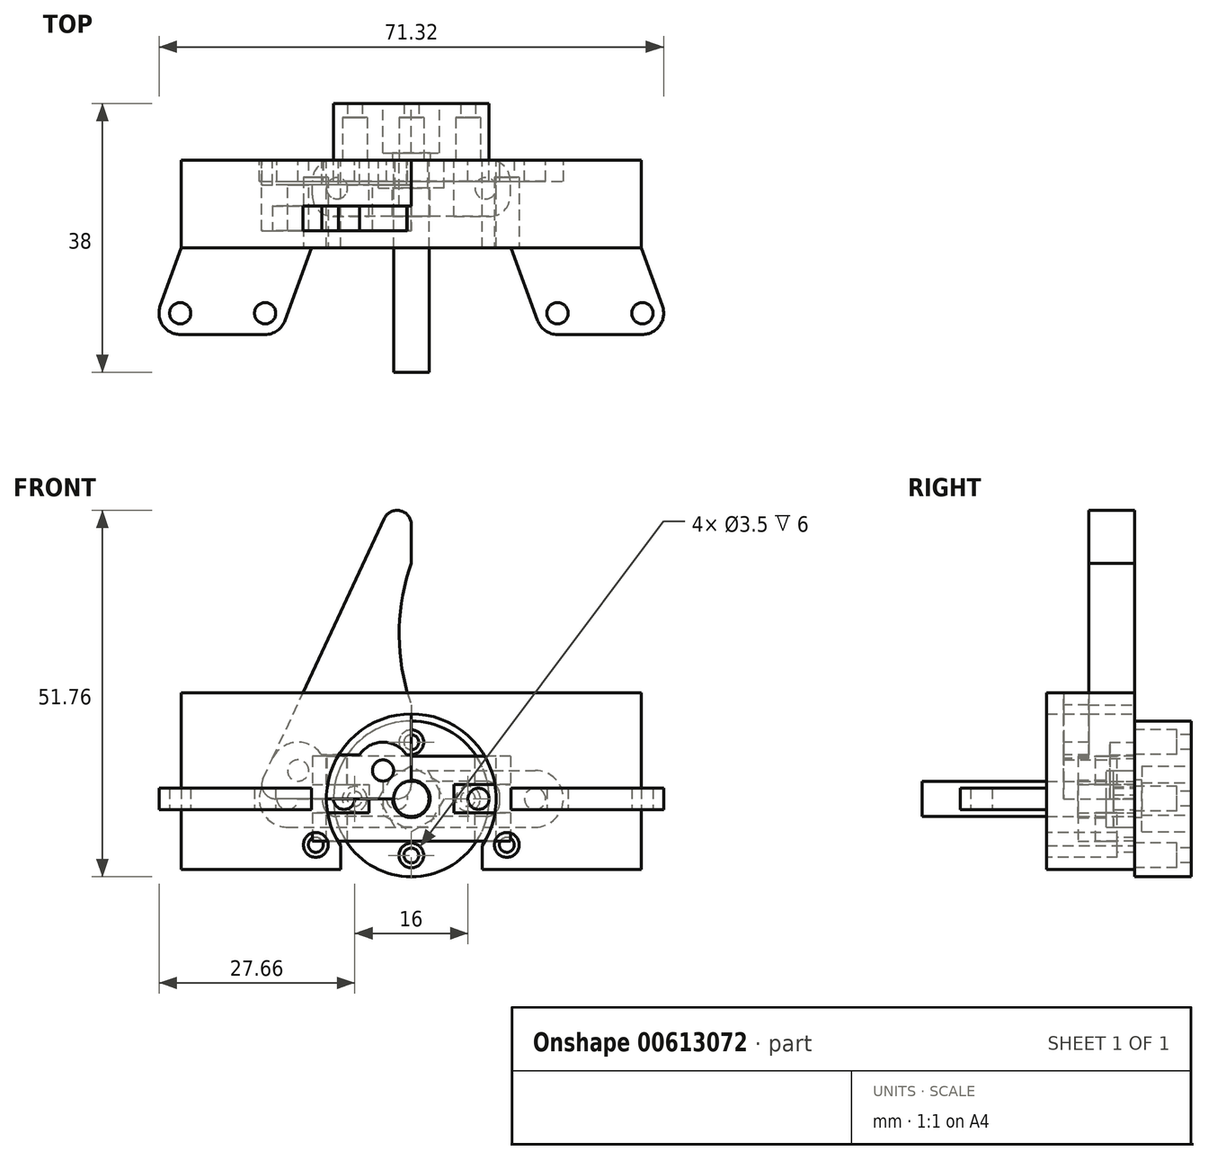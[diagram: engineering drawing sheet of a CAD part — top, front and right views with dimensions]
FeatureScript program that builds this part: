
annotation { "Feature Type Name" : "Feature", "Feature Type Description" : "" }
export const myFeature = defineFeature(function(context is Context, id is Id, definition is map)
    precondition{}
    {
        {
            var Q0;
            Q0=qCreatedBy(makeId("Front.planeOp"),FACE);
            var sketch = newSketch(context, id + "F0", { "sketchPlane" : qUnion([Q0])});
            skCircle(sketch, "E0", {"center": v(0, 0) * mm, "radius": 11 * mm});
            skCircle(sketch, "E1", {"center": v(0, 0) * mm, "radius": 8 * mm, "construction": true});
            skPoint(sketch, "E2", {"position": v(0, 8) * mm});
            skPoint(sketch, "E3", {"position": v(8, 0) * mm});
            skPoint(sketch, "E4", {"position": v(0, -8) * mm});
            skPoint(sketch, "E5", {"position": v(-8, 0) * mm});
            skSolve(sketch);
        }
        {
            var Q0;
            Q0=makeQuery(id+"F0.imprint","IMPRINT",FACE,{"disambiguationData":[TD([[makeQuery(id+"F0.imprint","IMPRINT",EDGE,{"derivedFrom":sQuery(id+"F0.wireOp",EDGE,"E0")}),1.0]])]});
            extrude(context, id + "F1", {"entities" : qUnion([Q0]), "oppositeDirection" : true, "depth" : 8 * mm, "offsetDistance" : 25 * mm});
        }
        {
            var Q0;
            Q0=sQuery(id+"F0.wireOp",VERTEX,"E2");
            var Q1;
            Q1=sQuery(id+"F0.wireOp",VERTEX,"E5");
            var Q2;
            Q2=sQuery(id+"F0.wireOp",VERTEX,"E4");
            var Q3;
            Q3=sQuery(id+"F0.wireOp",VERTEX,"E3");
            var Q4;
            Q4=makeQuery(id+"F1.opExtrude","SWEPT_BODY",BODY,{"disambiguationData":[OSD([sQuery(id+"F0.wireOp",EDGE,"E0")])]});
            hole(context, id + "F2", {"style" : HoleStyle.C_BORE, "endStyle" : HoleEndStyle.THROUGH, "holeDiameter" : 2.1 * mm, "cBoreDiameter" : 3.5 * mm, "cBoreDepth" : 6 * mm, "majorDiameter" : 5 * mm, "isTappedThrough" : true, "tappedDepth" : 12 * mm, "tapClearance" : 3, "locations" : qUnion([Q0, Q1, Q2, Q3]), "scope" : qUnion([Q4])});
        }
        {
            var Q0;
            Q0=sQuery(id+"F0.wireOp",VERTEX,"E0.center");
            var Q1;
            Q1=makeQuery(id+"F1.opExtrude","SWEPT_BODY",BODY,{"disambiguationData":[OSD([sQuery(id+"F0.wireOp",EDGE,"E0")])]});
            hole(context, id + "F3", {"style" : HoleStyle.SIMPLE, "endStyle" : HoleEndStyle.THROUGH, "holeDiameter" : 5.3 * mm, "majorDiameter" : 5 * mm, "isTappedThrough" : true, "tappedDepth" : 12 * mm, "tapClearance" : 3, "locations" : qUnion([Q0]), "scope" : qUnion([Q1])});
        }
        {
            var Q0;
            Q0=makeQuery(id+"F1.opExtrude","CAP_FACE",FACE,{"disambiguationData":[OSD([sQuery(id+"F0.wireOp",EDGE,"E0")])],"isStart":false});
            var sketch = newSketch(context, id + "F4", { "sketchPlane" : qUnion([Q0])});
            skLineSegment(sketch, "E6", {"start": v(0, -4.62) * mm, "end": v(-4, -2.3) * mm});
            skLineSegment(sketch, "E7", {"start": v(-4, -2.3) * mm, "end": v(-4, 2.3) * mm});
            skLineSegment(sketch, "E8", {"start": v(-4, 2.3) * mm, "end": v(0, 4.62) * mm});
            skLineSegment(sketch, "E9", {"start": v(0, 4.62) * mm, "end": v(4, 2.3) * mm});
            skLineSegment(sketch, "E10", {"start": v(4, 2.3) * mm, "end": v(4, -2.3) * mm});
            skLineSegment(sketch, "E11", {"start": v(4, -2.3) * mm, "end": v(0, -4.62) * mm});
            skSolve(sketch);
        }
        {
            var Q0;
            Q0=makeQuery(id+"F4.imprint","IMPRINT",FACE,{"disambiguationData":[TD([[makeQuery(id+"F4.imprint","IMPRINT",EDGE,{"derivedFrom":sQuery(id+"F4.wireOp",EDGE,"E6")}),-1.0]])]});
            extrude(context, id + "F5", {"entities" : qUnion([Q0]), "operationType" : NewBodyOperationType.REMOVE, "oppositeDirection" : true, "depth" : 7 * mm, "offsetDistance" : 25 * mm});
        }
        {
            var Q0;
            Q0=qCreatedBy(makeId("Front.planeOp"),FACE);
            var sketch = newSketch(context, id + "F6", { "sketchPlane" : qUnion([Q0])});
            skLineSegment(sketch, "E12", {"start": v(-14, -6) * mm, "end": v(14, -6) * mm});
            skLineSegment(sketch, "E13", {"start": v(14, 6) * mm, "end": v(-14, 6) * mm});
            skLineSegment(sketch, "E14", {"start": v(-14, 6) * mm, "end": v(-14, 2) * mm});
            skLineSegment(sketch, "E15", {"start": v(-14, 2) * mm, "end": v(-6, 2) * mm});
            skLineSegment(sketch, "E16", {"start": v(-6, 2) * mm, "end": v(-6, -2) * mm});
            skLineSegment(sketch, "E17", {"start": v(-6, -2) * mm, "end": v(-14, -2) * mm});
            skLineSegment(sketch, "E18", {"start": v(-14, -2) * mm, "end": v(-14, -6) * mm});
            skLineSegment(sketch, "E19", {"start": v(14, 6) * mm, "end": v(14, 2) * mm});
            skLineSegment(sketch, "E20", {"start": v(14, 2) * mm, "end": v(6, 2) * mm});
            skLineSegment(sketch, "E21", {"start": v(6, 2) * mm, "end": v(6, -2) * mm});
            skLineSegment(sketch, "E22", {"start": v(6, -2) * mm, "end": v(14, -2) * mm});
            skLineSegment(sketch, "E23", {"start": v(14, -2) * mm, "end": v(14, -6) * mm});
            skLineSegment(sketch, "E24", {"start": v(-4.62, 0) * mm, "end": v(-2.3, 4) * mm});
            skLineSegment(sketch, "E25", {"start": v(-2.3, 4) * mm, "end": v(2.3, 4) * mm});
            skLineSegment(sketch, "E26", {"start": v(2.3, 4) * mm, "end": v(4.62, 0) * mm});
            skLineSegment(sketch, "E27", {"start": v(4.62, 0) * mm, "end": v(2.3, -4) * mm});
            skLineSegment(sketch, "E28", {"start": v(2.3, -4) * mm, "end": v(-2.3, -4) * mm});
            skLineSegment(sketch, "E29", {"start": v(-2.3, -4) * mm, "end": v(-4.62, 0) * mm});
            skPoint(sketch, "E30", {"position": v(0, 0) * mm});
            skSolve(sketch);
        }
        {
            var Q0;
            Q0=makeQuery(id+"F6.imprint","IMPRINT",FACE,{"disambiguationData":[TD([[makeQuery(id+"F6.imprint","IMPRINT",EDGE,{"derivedFrom":sQuery(id+"F6.wireOp",EDGE,"E12")}),1.0]])]});
            var Q1;
            Q1=makeQuery(id+"F6.imprint","IMPRINT",FACE,{"disambiguationData":[TD([[makeQuery(id+"F6.imprint","IMPRINT",EDGE,{"derivedFrom":sQuery(id+"F6.wireOp",EDGE,"FAEP17WN-t7fj-iMpv-I29V-xNfxNTtkZkwR")}),-1.0]])]});
            var Q2;
            Q2=makeQuery(id+"F6.imprint","IMPRINT",FACE,{"disambiguationData":[TD([[makeQuery(id+"F6.imprint","IMPRINT",EDGE,{"derivedFrom":sQuery(id+"F6.wireOp",EDGE,"E24")}),-1.0]])]});
            extrude(context, id + "F7", {"entities" : qUnion([Q0, Q1, Q2]), "depth" : 8 * mm, "offsetDistance" : 25 * mm});
        }
        {
            var Q0;
            Q0=makeQuery(id+"F6.imprint","IMPRINT",FACE,{"disambiguationData":[TD([[makeQuery(id+"F6.imprint","IMPRINT",EDGE,{"derivedFrom":sQuery(id+"F6.wireOp",EDGE,"E24")}),-1.0]])]});
            extrude(context, id + "F8", {"entities" : qUnion([Q0]), "operationType" : NewBodyOperationType.REMOVE, "depth" : 4 * mm, "offsetDistance" : 25 * mm});
        }
        {
            var Q0;
            Q0=sQuery(id+"F6.wireOp",VERTEX,"E30");
            var Q1;
            Q1=makeQuery(id+"F7.opExtrude","SWEPT_BODY",BODY,{"disambiguationData":[OSD([sQuery(id+"F6.wireOp",EDGE,"E12"),sQuery(id+"F6.wireOp",EDGE,"E13"),sQuery(id+"F6.wireOp",EDGE,"E14"),sQuery(id+"F6.wireOp",EDGE,"E15"),sQuery(id+"F6.wireOp",EDGE,"E16"),sQuery(id+"F6.wireOp",EDGE,"E17"),sQuery(id+"F6.wireOp",EDGE,"E18"),sQuery(id+"F6.wireOp",EDGE,"E19"),sQuery(id+"F6.wireOp",EDGE,"E20"),sQuery(id+"F6.wireOp",EDGE,"E21"),sQuery(id+"F6.wireOp",EDGE,"E22"),sQuery(id+"F6.wireOp",EDGE,"E23")])]});
            hole(context, id + "F9", {"style" : HoleStyle.SIMPLE, "endStyle" : HoleEndStyle.THROUGH, "oppositeDirection" : true, "holeDiameter" : 5.3 * mm, "majorDiameter" : 5 * mm, "isTappedThrough" : true, "tappedDepth" : 12 * mm, "tapClearance" : 3, "locations" : qUnion([Q0]), "scope" : qUnion([Q1])});
        }
        {
            var Q0;
            Q0=qCreatedBy(makeId("Front.planeOp"),FACE);
            var sketch = newSketch(context, id + "F10", { "sketchPlane" : qUnion([Q0])});
            skCircle(sketch, "E31", {"center": v(0, 0) * mm, "radius": 2.5 * mm});
            skSolve(sketch);
        }
        {
            var Q0;
            Q0=makeQuery(id+"F10.imprint","IMPRINT",FACE,{"disambiguationData":[TD([[makeQuery(id+"F10.imprint","IMPRINT",EDGE,{"derivedFrom":sQuery(id+"F10.wireOp",EDGE,"E31")}),1.0]])]});
            extrude(context, id + "F11", {"entities" : qUnion([Q0]), "depth" : 30 * mm, "offsetDistance" : 25 * mm});
        }
        {
            var Q0;
            Q0=makeQuery(id+"F7.opExtrude","SWEPT_FACE",FACE,{"disambiguationData":[OSD([sQuery(id+"F6.wireOp",EDGE,"E13")])]});
            var sketch = newSketch(context, id + "F12", { "sketchPlane" : qUnion([Q0])});
            skPoint(sketch, "E32", {"position": v(10.5, -4) * mm});
            skPoint(sketch, "E33", {"position": v(-10.5, -4) * mm});
            skSolve(sketch);
        }
        {
            var Q0;
            Q0=sQuery(id+"F12.wireOp",VERTEX,"E33");
            var Q1;
            Q1=sQuery(id+"F12.wireOp",VERTEX,"E32");
            var Q2;
            Q2=makeQuery(id+"F7.opExtrude","SWEPT_BODY",BODY,{"disambiguationData":[OSD([sQuery(id+"F6.wireOp",EDGE,"E12"),sQuery(id+"F6.wireOp",EDGE,"E13"),sQuery(id+"F6.wireOp",EDGE,"E14"),sQuery(id+"F6.wireOp",EDGE,"E15"),sQuery(id+"F6.wireOp",EDGE,"E16"),sQuery(id+"F6.wireOp",EDGE,"E17"),sQuery(id+"F6.wireOp",EDGE,"E18"),sQuery(id+"F6.wireOp",EDGE,"E19"),sQuery(id+"F6.wireOp",EDGE,"E20"),sQuery(id+"F6.wireOp",EDGE,"E21"),sQuery(id+"F6.wireOp",EDGE,"E22"),sQuery(id+"F6.wireOp",EDGE,"E23")])]});
            hole(context, id + "F13", {"style" : HoleStyle.SIMPLE, "endStyle" : HoleEndStyle.THROUGH, "holeDiameter" : 3 * mm, "majorDiameter" : 5 * mm, "isTappedThrough" : true, "tappedDepth" : 12 * mm, "tapClearance" : 3, "locations" : qUnion([Q0, Q1]), "scope" : qUnion([Q2])});
        }
        {
            var Q0;
            Q0=qCreatedBy(makeId("Front.planeOp"),FACE);
            var sketch = newSketch(context, id + "F14", { "sketchPlane" : qUnion([Q0])});
            skLineSegment(sketch, "E34.bottom", {"start": v(10.5, -2.5) * mm, "end": v(-10.5, -2.5) * mm});
            skLineSegment(sketch, "E34.top", {"start": v(10.5, 2.5) * mm, "end": v(-10.5, 2.5) * mm});
            skLineSegment(sketch, "E34.left", {"start": v(12.5, -0.5) * mm, "end": v(12.5, 0.5) * mm});
            skLineSegment(sketch, "E34.right", {"start": v(-12.5, -0.5) * mm, "end": v(-12.5, 0.5) * mm});
            skPoint(sketch, "E34.middle", {"position": v(0, 0) * mm});
            skPoint(sketch, "E35.visualSharp", {"position": v(-12.5, 2.5) * mm});
            skArc(sketch, "E35.filletArc", {"start": v(-10.5, 2.5) * mm, "mid": v(-11.91, 1.91) * mm, "end": v(-12.5, 0.5) * mm});
            skPoint(sketch, "E36.visualSharp", {"position": v(-12.5, -2.5) * mm});
            skArc(sketch, "E36.filletArc", {"start": v(-12.5, -0.5) * mm, "mid": v(-11.91, -1.91) * mm, "end": v(-10.5, -2.5) * mm});
            skPoint(sketch, "E37.visualSharp", {"position": v(12.5, -2.5) * mm});
            skArc(sketch, "E37.filletArc", {"start": v(10.5, -2.5) * mm, "mid": v(11.91, -1.91) * mm, "end": v(12.5, -0.5) * mm});
            skPoint(sketch, "E38.visualSharp", {"position": v(12.5, 2.5) * mm});
            skArc(sketch, "E38.filletArc", {"start": v(12.5, 0.5) * mm, "mid": v(11.91, 1.91) * mm, "end": v(10.5, 2.5) * mm});
            skCircle(sketch, "E39", {"center": v(9.5, 0) * mm, "radius": 1.5 * mm});
            skPoint(sketch, "E39.centerSnap0", {"position": v(12.5, 0) * mm});
            skCircle(sketch, "E40", {"center": v(-9.5, 0) * mm, "radius": 1.5 * mm});
            skPoint(sketch, "E40.centerSnap0", {"position": v(-12.5, 0) * mm});
            skSolve(sketch);
        }
        {
            var Q0;
            Q0=makeQuery(id+"F14.imprint","IMPRINT",FACE,{"disambiguationData":[TD([[makeQuery(id+"F14.imprint","IMPRINT",EDGE,{"derivedFrom":sQuery(id+"F14.wireOp",EDGE,"E34.bottom")}),-1.0]])]});
            extrude(context, id + "F15", {"entities" : qUnion([Q0]), "depth" : 3 * mm, "offsetDistance" : 25 * mm});
        }
        {
            var Q0;
            Q0=makeQuery(id+"F7.opExtrude","CAP_EDGE",EDGE,{"disambiguationData":[OSD([sQuery(id+"F6.wireOp",EDGE,"E14")])],"isStart":false});
            var Q1;
            Q1=makeQuery(id+"F7.opExtrude","CAP_EDGE",EDGE,{"disambiguationData":[OSD([sQuery(id+"F6.wireOp",EDGE,"E18")])],"isStart":false});
            var Q2;
            Q2=makeQuery(id+"F7.opExtrude","CAP_EDGE",EDGE,{"disambiguationData":[OSD([sQuery(id+"F6.wireOp",EDGE,"E14")])],"isStart":true});
            var Q3;
            Q3=makeQuery(id+"F7.opExtrude","CAP_EDGE",EDGE,{"disambiguationData":[OSD([sQuery(id+"F6.wireOp",EDGE,"E18")])],"isStart":true});
            var Q4;
            Q4=makeQuery(id+"F7.opExtrude","CAP_EDGE",EDGE,{"disambiguationData":[OSD([sQuery(id+"F6.wireOp",EDGE,"E19")])],"isStart":true});
            var Q5;
            Q5=makeQuery(id+"F7.opExtrude","CAP_EDGE",EDGE,{"disambiguationData":[OSD([sQuery(id+"F6.wireOp",EDGE,"E23")])],"isStart":true});
            var Q6;
            Q6=makeQuery(id+"F7.opExtrude","CAP_EDGE",EDGE,{"disambiguationData":[OSD([sQuery(id+"F6.wireOp",EDGE,"E23")])],"isStart":false});
            var Q7;
            Q7=makeQuery(id+"F7.opExtrude","CAP_EDGE",EDGE,{"disambiguationData":[OSD([sQuery(id+"F6.wireOp",EDGE,"E19")])],"isStart":false});
            fillet(context, id + "F16", {"entities" : qUnion([Q0, Q1, Q2, Q3, Q4, Q5, Q6, Q7]), "radius" : 3 * mm, "tangentPropagation" : true, "allowEdgeOverflow" : false});
        }
        {
            var Q0;
            Q0=qCreatedBy(makeId("Front.planeOp"),FACE);
            var sketch = newSketch(context, id + "F17", { "sketchPlane" : qUnion([Q0])});
            skLineSegment(sketch, "E41", {"start": v(-17.5, 4) * mm, "end": v(17.5, 4) * mm});
            skLineSegment(sketch, "E42", {"start": v(-17.5, -4) * mm, "end": v(17.5, -4) * mm});
            skCircle(sketch, "E43", {"center": v(-17.5, 0) * mm, "radius": 1.5 * mm});
            skCircle(sketch, "E44", {"center": v(17.5, 0) * mm, "radius": 1.5 * mm});
            skCircle(sketch, "E45", {"center": v(-2, 0) * mm, "radius": 1.5 * mm});
            skArc(sketch, "E46", {"start": v(-17.5, -4) * mm, "mid": v(-21.5, 0) * mm, "end": v(-17.5, 4) * mm});
            skArc(sketch, "E47", {"start": v(17.5, -4) * mm, "mid": v(21.5, 0) * mm, "end": v(17.5, 4) * mm});
            skSolve(sketch);
        }
        {
            var Q0;
            Q0=makeQuery(id+"F17.imprint","IMPRINT",FACE,{"disambiguationData":[TD([[makeQuery(id+"F17.imprint","IMPRINT",EDGE,{"derivedFrom":sQuery(id+"F17.wireOp",EDGE,"E41")}),-1.0]])]});
            extrude(context, id + "F18", {"entities" : qUnion([Q0]), "depth" : 3 * mm, "offsetDistance" : 25 * mm});
        }
        {
            var Q0;
            Q0=qCreatedBy(makeId("Front.planeOp"),FACE);
            var sketch = newSketch(context, id + "F19", { "sketchPlane" : qUnion([Q0])});
            skCircle(sketch, "E48", {"center": v(0, 0) * mm, "radius": 12 * mm});
            skLineSegment(sketch, "E49", {"start": v(-10, -6.63) * mm, "end": v(-10, -32.5) * mm});
            skLineSegment(sketch, "E50", {"start": v(-10, -32.5) * mm, "end": v(10, -32.5) * mm, "construction": true});
            skLineSegment(sketch, "E51", {"start": v(10, -32.5) * mm, "end": v(10, -6.63) * mm});
            skPoint(sketch, "E52", {"position": v(13.5, -6.5) * mm});
            skPoint(sketch, "E53", {"position": v(13.5, -22.5) * mm});
            skPoint(sketch, "E54", {"position": v(-13.5, -22.5) * mm});
            skPoint(sketch, "E55", {"position": v(-13.5, -6.5) * mm});
            skLineSegment(sketch, "E56.top", {"start": v(32.5, 15) * mm, "end": v(-32.5, 15) * mm});
            skLineSegment(sketch, "E57", {"start": v(32.5, -10) * mm, "end": v(32.5, 15) * mm});
            skLineSegment(sketch, "E58", {"start": v(32.5, -10) * mm, "end": v(-32.5, -10) * mm});
            skLineSegment(sketch, "E59", {"start": v(-32.5, -10) * mm, "end": v(-32.5, 15) * mm});
            skSolve(sketch);
        }
        {
            var Q0;
            Q0=makeQuery(id+"F19.imprint","IMPRINT",FACE,{"disambiguationData":[TD([[makeQuery(id+"F19.imprint","IMPRINT",EDGE,{"derivedFrom":sQuery(id+"F19.wireOp",EDGE,"E56.top")}),1.0]])]});
            extrude(context, id + "F20", {"entities" : qUnion([Q0]), "depth" : 12.44 * mm, "offsetDistance" : 25 * mm});
        }
        {
            var Q0;
            Q0=qCreatedBy(makeId("Top.planeOp"),FACE);
            var sketch = newSketch(context, id + "F21", { "sketchPlane" : qUnion([Q0])});
            skLineSegment(sketch, "E60", {"start": v(32.5, 0) * mm, "end": v(32.5, -12.44) * mm});
            skLineSegment(sketch, "E61", {"start": v(32.5, -12.44) * mm, "end": v(-32.5, -12.44) * mm});
            skLineSegment(sketch, "E62", {"start": v(-32.5, -12.44) * mm, "end": v(-32.5, 0) * mm});
            skLineSegment(sketch, "E63", {"start": v(32.5, 0) * mm, "end": v(-32.5, 0) * mm});
            skLineSegment(sketch, "E64", {"start": v(14.11, -12.44) * mm, "end": v(18.56, -24.66) * mm});
            skLineSegment(sketch, "E65", {"start": v(18.56, -24.66) * mm, "end": v(36.95, -24.66) * mm});
            skLineSegment(sketch, "E66", {"start": v(36.95, -24.66) * mm, "end": v(32.5, -12.44) * mm});
            skLineSegment(sketch, "E67", {"start": v(-32.5, -12.44) * mm, "end": v(-36.95, -24.66) * mm});
            skLineSegment(sketch, "E68", {"start": v(-36.95, -24.66) * mm, "end": v(-18.56, -24.66) * mm});
            skLineSegment(sketch, "E69", {"start": v(-18.56, -24.66) * mm, "end": v(-14.11, -12.44) * mm});
            skPoint(sketch, "E70", {"position": v(20.66, -21.66) * mm});
            skPoint(sketch, "E71", {"position": v(32.66, -21.66) * mm});
            skPoint(sketch, "E72", {"position": v(-20.66, -21.66) * mm});
            skPoint(sketch, "E73", {"position": v(-32.66, -21.66) * mm});
            skSolve(sketch);
        }
        {
            var Q0;
            {var subQ2=sQuery(id+"F21.wireOp",EDGE,"E64");Q0=makeQuery(id+"F21.imprint","IMPRINT",FACE,{"disambiguationData":[TD([[makeQuery(id+"F21.imprint","IMPRINT",EDGE,{"derivedFrom":subQ2}),1.0]])]});}
            var Q1;
            {var subQ0=sQuery(id+"F21.wireOp",EDGE,"E67");Q1=makeQuery(id+"F21.imprint","IMPRINT",FACE,{"disambiguationData":[TD([[makeQuery(id+"F21.imprint","IMPRINT",EDGE,{"derivedFrom":subQ0}),1.0]])]});}
            extrude(context, id + "F22", {"entities" : qUnion([Q0, Q1]), "operationType" : NewBodyOperationType.ADD, "endBound" : BoundingType.SYMMETRIC, "depth" : 3 * mm, "offsetDistance" : 25 * mm});
        }
        {
            var Q0;
            {var subQ0=sQuery(id+"F19.wireOp",EDGE,"E56.left");var subQ1=sQuery(id+"F19.wireOp",EDGE,"E51");var subQ2=sQuery(id+"F19.wireOp",EDGE,"E56.bottom");var subQ3=sQuery(id+"F19.wireOp",EDGE,"E48");Q0=makeQuery(id+"F22.boolean.opBoolean","SPLIT",FACE,{"disambiguationData":[TD([makeQuery(id+"F20.opExtrude","SWEPT_FACE",FACE,{"disambiguationData":[OSD([subQ1])]})])],"derivedFrom":makeQuery(id+"F20.opExtrude","CAP_FACE",FACE,{"disambiguationData":[OSD([subQ3,sQuery(id+"F19.wireOp",EDGE,"E49"),subQ1,subQ2,sQuery(id+"F19.wireOp",EDGE,"E56.top"),subQ0,sQuery(id+"F19.wireOp",EDGE,"E56.right")])],"isStart":false})});}
            var sketch = newSketch(context, id + "F23", { "sketchPlane" : qUnion([Q0])});
            skPoint(sketch, "E74", {"position": v(13.5, -6.5) * mm});
            skPoint(sketch, "E75", {"position": v(-13.5, -6.5) * mm});
            skSolve(sketch);
        }
        {
            var Q0;
            Q0=sQuery(id+"F23.wireOp",VERTEX,"E74");
            var Q1;
            Q1=sQuery(id+"F23.wireOp",VERTEX,"E75");
            var Q2;
            Q2=makeQuery(id+"F20.opExtrude","SWEPT_BODY",BODY,{"disambiguationData":[OSD([sQuery(id+"F19.wireOp",EDGE,"E48"),sQuery(id+"F19.wireOp",EDGE,"E49"),sQuery(id+"F19.wireOp",EDGE,"E51"),sQuery(id+"F19.wireOp",EDGE,"E56.bottom"),sQuery(id+"F19.wireOp",EDGE,"E56.top"),sQuery(id+"F19.wireOp",EDGE,"E56.left"),sQuery(id+"F19.wireOp",EDGE,"E56.right")])]});
            hole(context, id + "F24", {"style" : HoleStyle.C_BORE, "endStyle" : HoleEndStyle.THROUGH, "holeDiameter" : 2.1 * mm, "cBoreDiameter" : 3.5 * mm, "cBoreDepth" : 10 * mm, "majorDiameter" : 5 * mm, "isTappedThrough" : true, "tappedDepth" : 12 * mm, "tapClearance" : 3, "locations" : qUnion([Q0, Q1]), "scope" : qUnion([Q2])});
        }
        {
            var Q0;
            Q0=sQuery(id+"F21.wireOp",VERTEX,"E70");
            var Q1;
            Q1=sQuery(id+"F21.wireOp",VERTEX,"E71");
            var Q2;
            Q2=makeQuery(id+"F20.opExtrude","SWEPT_BODY",BODY,{"disambiguationData":[OSD([sQuery(id+"F19.wireOp",EDGE,"E48"),sQuery(id+"F19.wireOp",EDGE,"E49"),sQuery(id+"F19.wireOp",EDGE,"E51"),sQuery(id+"F19.wireOp",EDGE,"E56.bottom"),sQuery(id+"F19.wireOp",EDGE,"E56.top"),sQuery(id+"F19.wireOp",EDGE,"E56.left"),sQuery(id+"F19.wireOp",EDGE,"E56.right")])]});
            hole(context, id + "F25", {"style" : HoleStyle.SIMPLE, "endStyle" : HoleEndStyle.THROUGH, "oppositeDirection" : true, "holeDiameter" : 3 * mm, "majorDiameter" : 5 * mm, "isTappedThrough" : true, "tappedDepth" : 12 * mm, "tapClearance" : 3, "locations" : qUnion([Q0, Q1]), "scope" : qUnion([Q2])});
        }
        {
            var Q0;
            Q0=sQuery(id+"F21.wireOp",VERTEX,"E70");
            var Q1;
            Q1=sQuery(id+"F21.wireOp",VERTEX,"E71");
            var Q2;
            Q2=makeQuery(id+"F20.opExtrude","SWEPT_BODY",BODY,{"disambiguationData":[OSD([sQuery(id+"F19.wireOp",EDGE,"E48"),sQuery(id+"F19.wireOp",EDGE,"E49"),sQuery(id+"F19.wireOp",EDGE,"E51"),sQuery(id+"F19.wireOp",EDGE,"E56.bottom"),sQuery(id+"F19.wireOp",EDGE,"E56.top"),sQuery(id+"F19.wireOp",EDGE,"E56.left"),sQuery(id+"F19.wireOp",EDGE,"E56.right")])]});
            hole(context, id + "F26", {"style" : HoleStyle.SIMPLE, "endStyle" : HoleEndStyle.THROUGH, "holeDiameter" : 3 * mm, "majorDiameter" : 5 * mm, "isTappedThrough" : true, "tappedDepth" : 12 * mm, "tapClearance" : 3, "locations" : qUnion([Q0, Q1]), "scope" : qUnion([Q2])});
        }
        {
            var Q0;
            Q0=sQuery(id+"F21.wireOp",VERTEX,"E72");
            var Q1;
            Q1=sQuery(id+"F21.wireOp",VERTEX,"E73");
            var Q2;
            Q2=makeQuery(id+"F20.opExtrude","SWEPT_BODY",BODY,{"disambiguationData":[OSD([sQuery(id+"F19.wireOp",EDGE,"E48"),sQuery(id+"F19.wireOp",EDGE,"E49"),sQuery(id+"F19.wireOp",EDGE,"E51"),sQuery(id+"F19.wireOp",EDGE,"E56.bottom"),sQuery(id+"F19.wireOp",EDGE,"E56.top"),sQuery(id+"F19.wireOp",EDGE,"E56.left"),sQuery(id+"F19.wireOp",EDGE,"E56.right")])]});
            hole(context, id + "F27", {"style" : HoleStyle.SIMPLE, "endStyle" : HoleEndStyle.THROUGH, "oppositeDirection" : true, "holeDiameter" : 3 * mm, "majorDiameter" : 5 * mm, "isTappedThrough" : true, "tappedDepth" : 12 * mm, "tapClearance" : 3, "locations" : qUnion([Q0, Q1]), "scope" : qUnion([Q2])});
        }
        {
            var Q0;
            Q0=sQuery(id+"F21.wireOp",VERTEX,"E72");
            var Q1;
            Q1=sQuery(id+"F21.wireOp",VERTEX,"E73");
            var Q2;
            Q2=makeQuery(id+"F20.opExtrude","SWEPT_BODY",BODY,{"disambiguationData":[OSD([sQuery(id+"F19.wireOp",EDGE,"E48"),sQuery(id+"F19.wireOp",EDGE,"E49"),sQuery(id+"F19.wireOp",EDGE,"E51"),sQuery(id+"F19.wireOp",EDGE,"E56.bottom"),sQuery(id+"F19.wireOp",EDGE,"E56.top"),sQuery(id+"F19.wireOp",EDGE,"E56.left"),sQuery(id+"F19.wireOp",EDGE,"E56.right")])]});
            hole(context, id + "F28", {"style" : HoleStyle.SIMPLE, "endStyle" : HoleEndStyle.THROUGH, "holeDiameter" : 3 * mm, "majorDiameter" : 5 * mm, "isTappedThrough" : true, "tappedDepth" : 12 * mm, "tapClearance" : 3, "locations" : qUnion([Q0, Q1]), "scope" : qUnion([Q2])});
        }
        {
            var Q0;
            Q0=makeQuery(id+"F22.opExtrude","SWEPT_EDGE",EDGE,{"disambiguationData":[OSD([sQuery(id+"F21.wireOp",EDGE,"E65"),sQuery(id+"F21.wireOp",EDGE,"E66")])]});
            var Q1;
            Q1=makeQuery(id+"F22.opExtrude","SWEPT_EDGE",EDGE,{"disambiguationData":[OSD([sQuery(id+"F21.wireOp",EDGE,"E64"),sQuery(id+"F21.wireOp",EDGE,"E65")])]});
            var Q2;
            Q2=makeQuery(id+"F22.opExtrude","SWEPT_EDGE",EDGE,{"disambiguationData":[OSD([sQuery(id+"F21.wireOp",EDGE,"E68"),sQuery(id+"F21.wireOp",EDGE,"E69")])]});
            var Q3;
            Q3=makeQuery(id+"F22.opExtrude","SWEPT_EDGE",EDGE,{"disambiguationData":[OSD([sQuery(id+"F21.wireOp",EDGE,"E67"),sQuery(id+"F21.wireOp",EDGE,"E68")])]});
            fillet(context, id + "F29", {"entities" : qUnion([Q0, Q1, Q2, Q3]), "radius" : 3 * mm, "tangentPropagation" : true, "allowEdgeOverflow" : false});
        }
        {
            var Q0;
            Q0=qCreatedBy(makeId("Front.planeOp"),FACE);
            var sketch = newSketch(context, id + "F30", { "sketchPlane" : qUnion([Q0])});
            skLineSegment(sketch, "E76", {"start": v(0, 38.76) * mm, "end": v(0, 2) * mm});
            skLineSegment(sketch, "E77", {"start": v(-2, 0) * mm, "end": v(-19.14, 0) * mm});
            skLineSegment(sketch, "E78", {"start": v(-20.95, 2.85) * mm, "end": v(-3.81, 39.6) * mm});
            skPoint(sketch, "E79", {"position": v(-4, 4) * mm});
            skPoint(sketch, "E80", {"position": v(-16, 4) * mm});
            skPoint(sketch, "E81.visualSharp", {"position": v(0, 47.78) * mm});
            skArc(sketch, "E81.filletArc", {"start": v(0, 38.76) * mm, "mid": v(-1.57, 40.7) * mm, "end": v(-3.81, 39.6) * mm});
            skPoint(sketch, "E82.visualSharp", {"position": v(-22.28, 0) * mm});
            skArc(sketch, "E82.filletArc", {"start": v(-20.95, 2.85) * mm, "mid": v(-20.83, 0.93) * mm, "end": v(-19.14, 0) * mm});
            skPoint(sketch, "E83.visualSharp", {"position": v(0, 0) * mm});
            skArc(sketch, "E83.filletArc", {"start": v(-2, 0) * mm, "mid": v(-0.59, 0.59) * mm, "end": v(0, 2) * mm});
            skArc(sketch, "E84", {"start": v(-19.63, 5.7) * mm, "mid": v(-16.3, 7.99) * mm, "end": v(-12.66, 6.2) * mm});
            skArc(sketch, "E85", {"start": v(-7.34, 6.2) * mm, "mid": v(-4, 8) * mm, "end": v(-0.66, 6.2) * mm});
            skLineSegment(sketch, "E86", {"start": v(-7.34, 6.2) * mm, "end": v(-12.66, 6.2) * mm});
            skArc(sketch, "E87", {"start": v(0, 33.26) * mm, "mid": v(-1.72, 23.26) * mm, "end": v(0, 13.26) * mm});
            skLineSegment(sketch, "E88", {"start": v(-0.66, 6.2) * mm, "end": v(0, 6.2) * mm});
            skSolve(sketch);
        }
        {
            var Q0;
            {var subQ0=sQuery(id+"F30.wireOp",EDGE,"E81.filletArc");Q0=makeQuery(id+"F30.imprint","IMPRINT",FACE,{"disambiguationData":[TD([[makeQuery(id+"F30.imprint","IMPRINT",EDGE,{"derivedFrom":subQ0}),1.0]])]});}
            var Q1;
            Q1=makeQuery(id+"F30.imprint","IMPRINT",FACE,{"disambiguationData":[TD([[makeQuery(id+"F30.imprint","IMPRINT",EDGE,{"derivedFrom":sQuery(id+"F30.wireOp",EDGE,"E77")}),-1.0]])]});
            extrude(context, id + "F31", {"entities" : qUnion([Q0, Q1]), "depth" : 10 * mm, "offsetDistance" : 25 * mm});
        }
        {
            var Q0;
            Q0=sQuery(id+"F30.wireOp",VERTEX,"E79");
            var Q1;
            Q1=sQuery(id+"F30.wireOp",VERTEX,"E80");
            var Q2;
            Q2=makeQuery(id+"F31.opExtrude","SWEPT_BODY",BODY,{"disambiguationData":[OSD([sQuery(id+"F30.wireOp",EDGE,"E76"),sQuery(id+"F30.wireOp",EDGE,"E77"),sQuery(id+"F30.wireOp",EDGE,"E78"),sQuery(id+"F30.wireOp",EDGE,"E81.filletArc"),sQuery(id+"F30.wireOp",EDGE,"E82.filletArc"),sQuery(id+"F30.wireOp",EDGE,"E83.filletArc")])]});
            hole(context, id + "F32", {"style" : HoleStyle.SIMPLE, "endStyle" : HoleEndStyle.THROUGH, "oppositeDirection" : true, "holeDiameter" : 3 * mm, "majorDiameter" : 5 * mm, "isTappedThrough" : true, "tappedDepth" : 12 * mm, "tapClearance" : 3, "locations" : qUnion([Q0, Q1]), "scope" : qUnion([Q2])});
        }
        {
            var Q0;
            Q0=makeQuery(id+"F31.opExtrude","CAP_FACE",FACE,{"disambiguationData":[OSD([sQuery(id+"F30.wireOp",EDGE,"E76"),sQuery(id+"F30.wireOp",EDGE,"E77"),sQuery(id+"F30.wireOp",EDGE,"E78"),sQuery(id+"F30.wireOp",EDGE,"E81.filletArc"),sQuery(id+"F30.wireOp",EDGE,"E82.filletArc"),sQuery(id+"F30.wireOp",EDGE,"E83.filletArc")])],"isStart":false});
            var sketch = newSketch(context, id + "F33", { "sketchPlane" : qUnion([Q0])});
            skArc(sketch, "E89", {"start": v(-19.63, 5.7) * mm, "mid": v(-16.3, 7.99) * mm, "end": v(-12.66, 6.2) * mm});
            skArc(sketch, "E90", {"start": v(-7.34, 6.2) * mm, "mid": v(-4, 8) * mm, "end": v(-0.66, 6.2) * mm});
            skLineSegment(sketch, "E91", {"start": v(-12.66, 6.2) * mm, "end": v(-7.34, 6.2) * mm});
            skLineSegment(sketch, "E92", {"start": v(-0.66, 6.2) * mm, "end": v(0, 6.2) * mm});
            skSolve(sketch);
        }
        {
            var Q0;
            {var subQ2=sQuery(id+"F33.wireOp",EDGE,"E89");Q0=makeQuery(id+"F33.imprint","IMPRINT",FACE,{"disambiguationData":[TD([[makeQuery(id+"F33.imprint","IMPRINT",EDGE,{"derivedFrom":subQ2}),-1.0]])]});}
            extrude(context, id + "F34", {"entities" : qUnion([Q0]), "operationType" : NewBodyOperationType.REMOVE, "oppositeDirection" : true, "depth" : 3.5 * mm, "offsetDistance" : 25 * mm});
        }
        {
            var Q0;
            Q0=makeQuery(id+"F30.imprint","IMPRINT",FACE,{"disambiguationData":[TD([[makeQuery(id+"F30.imprint","IMPRINT",EDGE,{"derivedFrom":sQuery(id+"F30.wireOp",EDGE,"E77")}),-1.0]])]});
            extrude(context, id + "F35", {"entities" : qUnion([Q0]), "operationType" : NewBodyOperationType.REMOVE, "depth" : 3.5 * mm, "offsetDistance" : 25 * mm});
        }
    });
